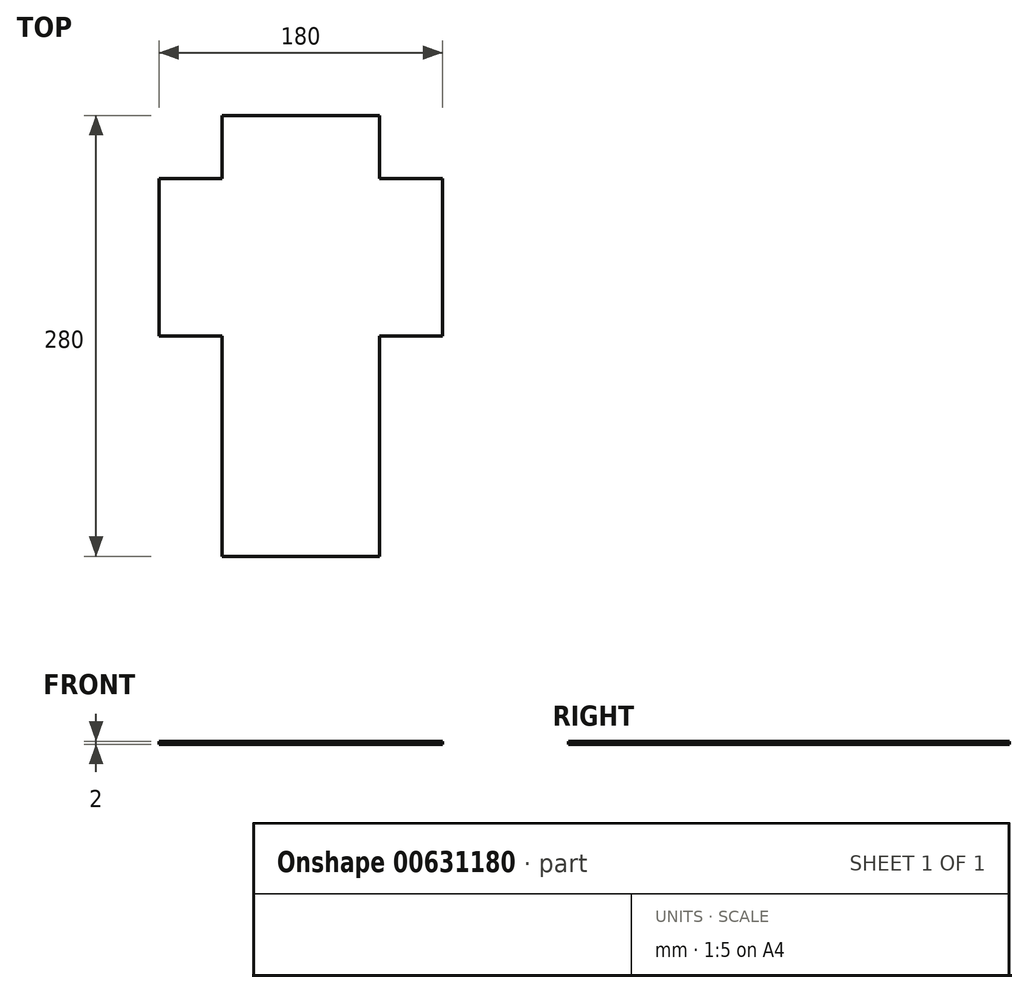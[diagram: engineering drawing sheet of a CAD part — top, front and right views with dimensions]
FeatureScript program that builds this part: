
annotation { "Feature Type Name" : "Feature", "Feature Type Description" : "" }
export const myFeature = defineFeature(function(context is Context, id is Id, definition is map)
    precondition{}
    {
        {
            var Q0;
            Q0=qCreatedBy(makeId("Top.planeOp"),FACE);
            var sketch = newSketch(context, id + "F0", { "sketchPlane" : qUnion([Q0])});
            skLineSegment(sketch, "E0.bottom", {"start": v(0, 0) * mm, "end": v(100, 0) * mm});
            skLineSegment(sketch, "E0.top", {"start": v(0, 100) * mm, "end": v(100, 100) * mm});
            skLineSegment(sketch, "E0.left", {"start": v(0, 0) * mm, "end": v(0, 100) * mm});
            skLineSegment(sketch, "E0.right", {"start": v(100, 0) * mm, "end": v(100, 100) * mm});
            skLineSegment(sketch, "E1.top", {"start": v(0, -40) * mm, "end": v(100, -40) * mm});
            skLineSegment(sketch, "E1.left", {"start": v(0, 0) * mm, "end": v(0, -40) * mm});
            skLineSegment(sketch, "E1.right", {"start": v(100, 0) * mm, "end": v(100, -40) * mm});
            skLineSegment(sketch, "E2.top", {"start": v(0, -140) * mm, "end": v(100, -140) * mm});
            skLineSegment(sketch, "E2.left", {"start": v(0, -40) * mm, "end": v(0, -140) * mm});
            skLineSegment(sketch, "E2.right", {"start": v(100, -40) * mm, "end": v(100, -140) * mm});
            skLineSegment(sketch, "E3.bottom", {"start": v(0, 0) * mm, "end": v(-40, 0) * mm});
            skLineSegment(sketch, "E3.top", {"start": v(0, 100) * mm, "end": v(-40, 100) * mm});
            skLineSegment(sketch, "E3.right", {"start": v(-40, 0) * mm, "end": v(-40, 100) * mm});
            skLineSegment(sketch, "E4.bottom", {"start": v(100, 0) * mm, "end": v(140, 0) * mm});
            skLineSegment(sketch, "E4.top", {"start": v(100, 100) * mm, "end": v(140, 100) * mm});
            skLineSegment(sketch, "E4.right", {"start": v(140, 0) * mm, "end": v(140, 100) * mm});
            skLineSegment(sketch, "E5.top", {"start": v(0, 140) * mm, "end": v(100, 140) * mm});
            skLineSegment(sketch, "E5.left", {"start": v(0, 100) * mm, "end": v(0, 140) * mm});
            skLineSegment(sketch, "E5.right", {"start": v(100, 100) * mm, "end": v(100, 140) * mm});
            skSolve(sketch);
        }
        {
            var Q0;
            Q0 = qSketchRegion(id + "F0", true);
            extrude(context, id + "F1", {"entities" : qUnion([Q0]), "depth" : 2 * mm, "offsetDistance" : 25 * mm});
        }
    });
